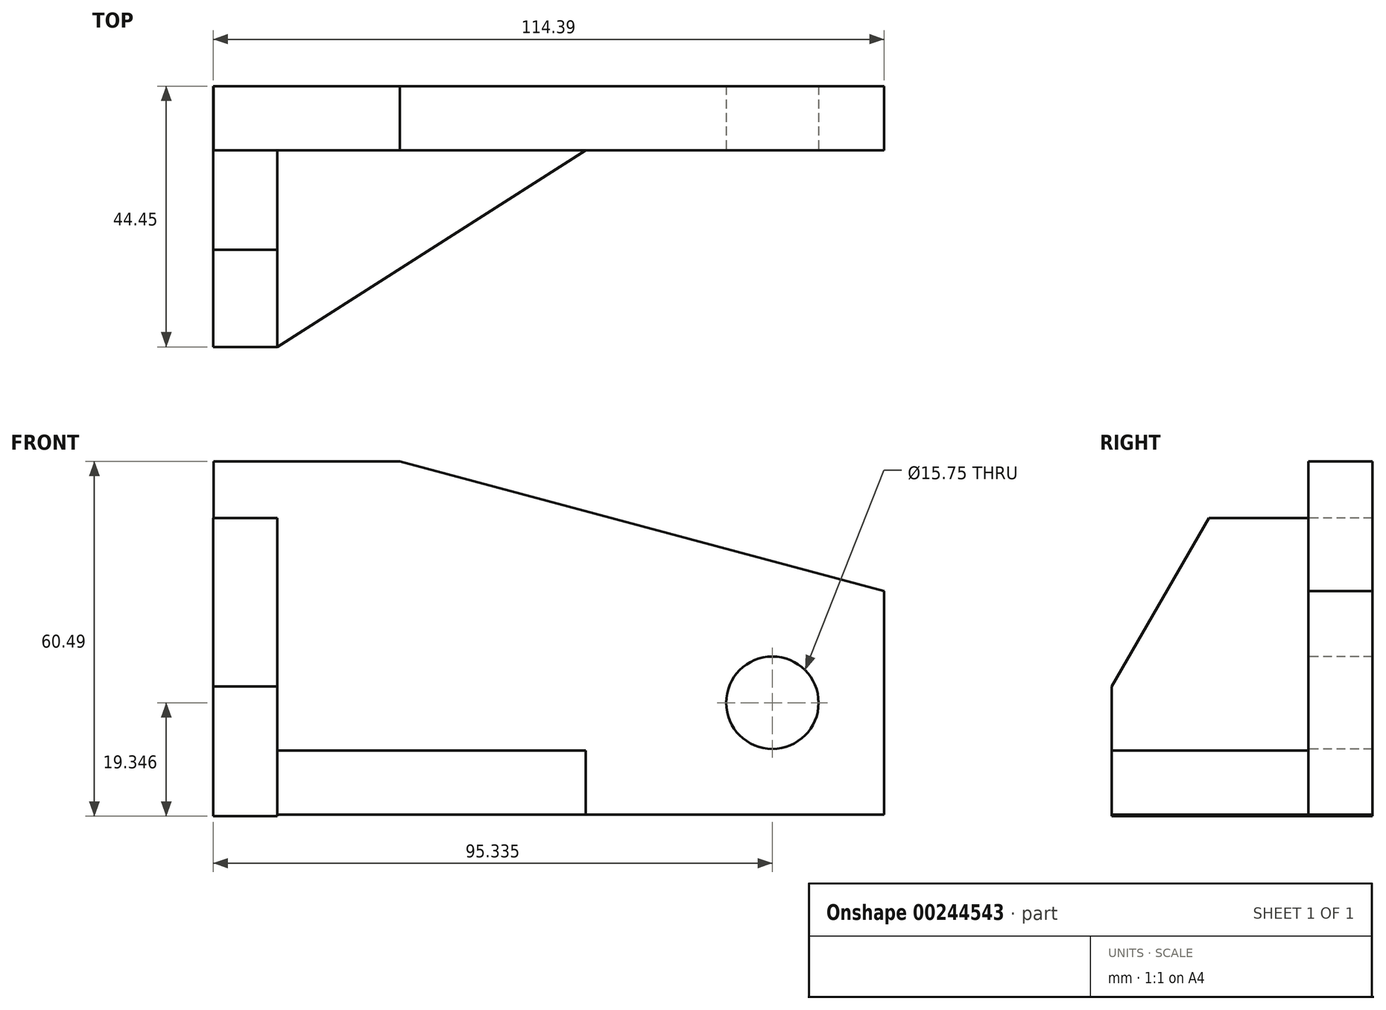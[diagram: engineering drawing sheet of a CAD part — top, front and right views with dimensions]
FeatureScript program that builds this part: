
annotation { "Feature Type Name" : "Feature", "Feature Type Description" : "" }
export const myFeature = defineFeature(function(context is Context, id is Id, definition is map)
    precondition{}
    {
        {
            var Q0;
            Q0=qCreatedBy(makeId("Front.planeOp"),FACE);
            var sketch = newSketch(context, id + "F0", { "sketchPlane" : qUnion([Q0])});
            skLineSegment(sketch, "E0.top", {"start": v(-38.01, -32.03) * mm, "end": v(76.29, -32.03) * mm});
            skLineSegment(sketch, "E0.left", {"start": v(-38.01, 28.16) * mm, "end": v(-38.01, -32.03) * mm});
            skLineSegment(sketch, "E0.right", {"start": v(76.29, 28.16) * mm, "end": v(76.29, -32.03) * mm});
            skPoint(sketch, "E1", {"position": v(-6.26, 28.16) * mm});
            skLineSegment(sketch, "E2", {"start": v(-38.01, 28.16) * mm, "end": v(-6.26, 28.16) * mm});
            skLineSegment(sketch, "E3", {"start": v(-6.26, 28.16) * mm, "end": v(76.29, 28.16) * mm});
            skLineSegment(sketch, "E4", {"start": v(-6.26, 28.16) * mm, "end": v(76.29, 6.04) * mm});
            skSolve(sketch);
        }
        {
            var Q0;
            {var subQ1=sQuery(id+"F0.wireOp",EDGE,"E0.top");Q0=makeQuery(id+"F0.imprint","IMPRINT",FACE,{"disambiguationData":[TD([[makeQuery(id+"F0.imprint","IMPRINT",EDGE,{"derivedFrom":subQ1}),1.0]])]});}
            extrude(context, id + "F1", {"entities" : qUnion([Q0]), "depth" : 10.92 * mm});
        }
        {
            var Q0;
            Q0=qCreatedBy(makeId("Front.planeOp"),FACE);
            var sketch = newSketch(context, id + "F2", { "sketchPlane" : qUnion([Q0])});
            skLineSegment(sketch, "E5.bottom", {"start": v(-38.1, -32.33) * mm, "end": v(-27.18, -32.33) * mm});
            skLineSegment(sketch, "E5.top", {"start": v(-38.1, 18.47) * mm, "end": v(-27.18, 18.47) * mm});
            skLineSegment(sketch, "E5.left", {"start": v(-38.1, -32.33) * mm, "end": v(-38.1, 18.47) * mm});
            skLineSegment(sketch, "E5.right", {"start": v(-27.18, -32.33) * mm, "end": v(-27.18, 18.47) * mm});
            skSolve(sketch);
        }
        {
            var Q0;
            Q0 = qSketchRegion(id + "F2", true);
            extrude(context, id + "F3", {"entities" : qUnion([Q0]), "operationType" : NewBodyOperationType.ADD, "depth" : 44.45 * mm});
        }
        {
            var Q0;
            Q0=makeQuery(id+"F3.opExtrude","SWEPT_FACE",FACE,{"disambiguationData":[OSD([sQuery(id+"F2.wireOp",EDGE,"E5.right")])]});
            var sketch = newSketch(context, id + "F4", { "sketchPlane" : qUnion([Q0])});
            skPoint(sketch, "E6", {"position": v(-44.45, -10.23) * mm});
            skLineSegment(sketch, "E7", {"start": v(-44.45, -10.23) * mm, "end": v(-27.88, 18.47) * mm});
            skSolve(sketch);
        }
        {
            var Q0;
            {var subQ0=sQuery(id+"F4.wireOp",EDGE,"E7");Q0=makeQuery(id+"F4.imprint","IMPRINT",FACE,{"disambiguationData":[TD([[makeQuery(id+"F4.imprint","IMPRINT",EDGE,{"derivedFrom":subQ0}),1.0]])]});}
            extrude(context, id + "F5", {"entities" : qUnion([Q0]), "operationType" : NewBodyOperationType.REMOVE, "endBound" : BoundingType.THROUGH_ALL, "oppositeDirection" : true, "depth" : 25.4 * mm});
        }
        {
            var Q0;
            Q0=makeQuery(id+"F1.opExtrude","CAP_FACE",FACE,{"disambiguationData":[OSD([sQuery(id+"F0.wireOp",EDGE,"E0.top"),sQuery(id+"F0.wireOp",EDGE,"E0.left"),sQuery(id+"F0.wireOp",EDGE,"E0.right"),sQuery(id+"F0.wireOp",EDGE,"E2"),sQuery(id+"F0.wireOp",EDGE,"E4")])],"isStart":false});
            var sketch = newSketch(context, id + "F6", { "sketchPlane" : qUnion([Q0])});
            skLineSegment(sketch, "E8.bottom", {"start": v(-27.18, -32.03) * mm, "end": v(25.4, -32.03) * mm});
            skLineSegment(sketch, "E8.top", {"start": v(-27.18, -21.11) * mm, "end": v(25.4, -21.11) * mm});
            skLineSegment(sketch, "E8.left", {"start": v(-27.18, -32.03) * mm, "end": v(-27.18, -21.11) * mm});
            skLineSegment(sketch, "E8.right", {"start": v(25.4, -32.03) * mm, "end": v(25.4, -21.11) * mm});
            skSolve(sketch);
        }
        {
            var Q0;
            Q0=makeQuery(id+"F6.imprint","IMPRINT",FACE,{"disambiguationData":[TD([[makeQuery(id+"F6.imprint","IMPRINT",EDGE,{"derivedFrom":sQuery(id+"F6.wireOp",EDGE,"E8.bottom")}),1.0]])]});
            extrude(context, id + "F7", {"entities" : qUnion([Q0]), "operationType" : NewBodyOperationType.ADD, "depth" : 33.53 * mm});
        }
        {
            var Q0;
            Q0=makeQuery(id+"F7.opExtrude","SWEPT_FACE",FACE,{"disambiguationData":[OSD([sQuery(id+"F6.wireOp",EDGE,"E8.top")])]});
            var sketch = newSketch(context, id + "F8", { "sketchPlane" : qUnion([Q0])});
            skLineSegment(sketch, "E9", {"start": v(-27.18, -44.45) * mm, "end": v(25.4, -10.92) * mm});
            skSolve(sketch);
        }
        {
            var Q0;
            Q0=makeQuery(id+"F8.imprint","IMPRINT",FACE,{"disambiguationData":[TD([[makeQuery(id+"F8.imprint","IMPRINT",EDGE,{"derivedFrom":sQuery(id+"F8.wireOp",EDGE,"E9")}),-1.0]])]});
            extrude(context, id + "F9", {"entities" : qUnion([Q0]), "operationType" : NewBodyOperationType.REMOVE, "endBound" : BoundingType.THROUGH_ALL, "oppositeDirection" : true, "depth" : 25.4 * mm});
        }
        {
            var Q0;
            Q0=makeQuery(id+"F1.opExtrude","CAP_FACE",FACE,{"disambiguationData":[OSD([sQuery(id+"F0.wireOp",EDGE,"E0.top"),sQuery(id+"F0.wireOp",EDGE,"E0.left"),sQuery(id+"F0.wireOp",EDGE,"E0.right"),sQuery(id+"F0.wireOp",EDGE,"E2"),sQuery(id+"F0.wireOp",EDGE,"E4")])],"isStart":false});
            var sketch = newSketch(context, id + "F10", { "sketchPlane" : qUnion([Q0])});
            skPoint(sketch, "E10", {"position": v(57.24, -12.98) * mm});
            skSolve(sketch);
        }
        {
            var Q0;
            Q0=sQuery(id+"F10.wireOp",VERTEX,"E10");
            var Q1;
            Q1=makeQuery(id+"F1.opExtrude","SWEPT_BODY",BODY,{"disambiguationData":[OSD([sQuery(id+"F0.wireOp",EDGE,"E0.top"),sQuery(id+"F0.wireOp",EDGE,"E0.left"),sQuery(id+"F0.wireOp",EDGE,"E0.right"),sQuery(id+"F0.wireOp",EDGE,"E2"),sQuery(id+"F0.wireOp",EDGE,"E4")])]});
            hole(context, id + "F11", {"style" : HoleStyle.SIMPLE, "endStyle" : HoleEndStyle.THROUGH, "holeDiameter" : 15.75 * mm, "tappedDepth" : 12.7 * mm, "tapClearance" : 3, "locations" : qUnion([Q0]), "scope" : qUnion([Q1])});
        }
    });
